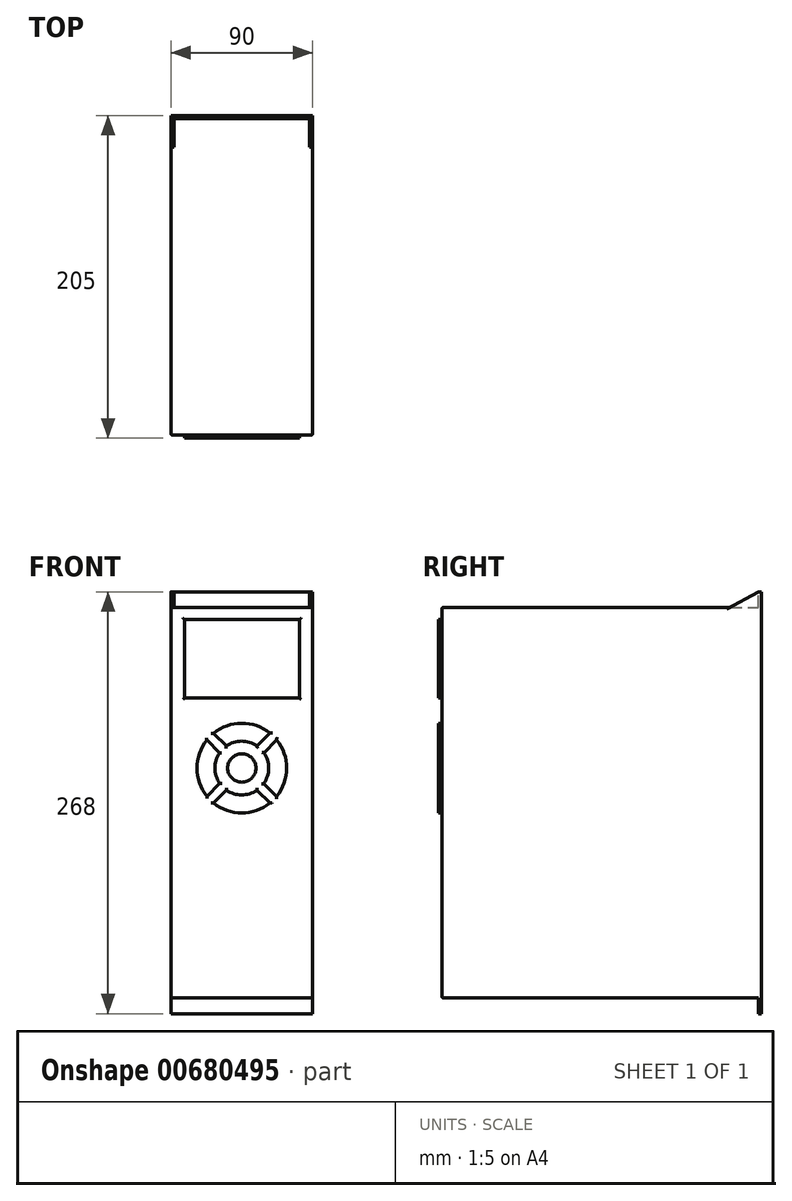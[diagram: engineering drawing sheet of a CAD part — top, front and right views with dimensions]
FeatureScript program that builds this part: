
annotation { "Feature Type Name" : "Feature", "Feature Type Description" : "" }
export const myFeature = defineFeature(function(context is Context, id is Id, definition is map)
    precondition{}
    {
        {
            var Q0;
            Q0=qCreatedBy(makeId("Front.planeOp"),FACE);
            var sketch = newSketch(context, id + "F0", { "sketchPlane" : qUnion([Q0])});
            skLineSegment(sketch, "E0.bottom", {"start": v(45, 124) * mm, "end": v(-45, 124) * mm});
            skLineSegment(sketch, "E0.top", {"start": v(45, -124) * mm, "end": v(-45, -124) * mm});
            skLineSegment(sketch, "E0.left", {"start": v(45, 124) * mm, "end": v(45, -124) * mm});
            skLineSegment(sketch, "E0.right", {"start": v(-45, 124) * mm, "end": v(-45, -124) * mm});
            skPoint(sketch, "E0.middle", {"position": v(0, 0) * mm});
            skSolve(sketch);
        }
        {
            var Q0;
            Q0=makeQuery(id+"F0.imprint","IMPRINT",FACE,{"disambiguationData":[TD([[makeQuery(id+"F0.imprint","IMPRINT",EDGE,{"derivedFrom":sQuery(id+"F0.wireOp",EDGE,"E0.bottom")}),1.0]])]});
            extrude(context, id + "F1", {"entities" : qUnion([Q0]), "depth" : 205 * mm, "offsetDistance" : 25 * mm});
        }
        {
            var Q0;
            Q0=makeQuery(id+"F1.opExtrude","CAP_FACE",FACE,{"disambiguationData":[OSD([sQuery(id+"F0.wireOp",EDGE,"E0.bottom"),sQuery(id+"F0.wireOp",EDGE,"E0.top"),sQuery(id+"F0.wireOp",EDGE,"E0.left"),sQuery(id+"F0.wireOp",EDGE,"E0.right")])],"isStart":false});
            var sketch = newSketch(context, id + "F2", { "sketchPlane" : qUnion([Q0])});
            skLineSegment(sketch, "E1.bottom", {"start": v(-36.41, 116.3) * mm, "end": v(36.68, 116.3) * mm});
            skLineSegment(sketch, "E1.top", {"start": v(-36.41, 66.5) * mm, "end": v(36.68, 66.5) * mm});
            skLineSegment(sketch, "E1.left", {"start": v(-36.41, 116.3) * mm, "end": v(-36.41, 66.5) * mm});
            skLineSegment(sketch, "E1.right", {"start": v(36.68, 116.3) * mm, "end": v(36.68, 66.5) * mm});
            skArc(sketch, "E2", {"start": v(-22.23, 39.81) * mm, "mid": v(-28.49, 21.94) * mm, "end": v(-22.15, 4.09) * mm});
            skLineSegment(sketch, "E3.0", {"start": v(22.18, 3.89) * mm, "end": v(13.93, 12.13) * mm});
            skLineSegment(sketch, "E4.0", {"start": v(17.93, -0.36) * mm, "end": v(9.66, 7.92) * mm});
            skLineSegment(sketch, "E5.0", {"start": v(-18.11, -0.36) * mm, "end": v(-9.76, 8) * mm});
            skLineSegment(sketch, "E6.0", {"start": v(-22.36, 3.89) * mm, "end": v(-14, 12.24) * mm});
            skArc(sketch, "E7.trimOffspring", {"start": v(17.91, 44.15) * mm, "mid": v(-0.06, 50.49) * mm, "end": v(-18, 44.07) * mm});
            skArc(sketch, "E8.trimOffspring", {"start": v(-17.91, -0.15) * mm, "mid": v(-0.06, -6.49) * mm, "end": v(17.81, -0.23) * mm});
            skArc(sketch, "E9.trimOffspring", {"start": v(22.07, 4) * mm, "mid": v(28.49, 21.94) * mm, "end": v(22.15, 39.91) * mm});
            skLineSegment(sketch, "E10.trimOffspring", {"start": v(-14.08, 31.66) * mm, "end": v(-22.36, 39.93) * mm});
            skLineSegment(sketch, "E11.trimOffspring", {"start": v(14, 31.76) * mm, "end": v(22.18, 39.93) * mm});
            skLineSegment(sketch, "E12.trimOffspring", {"start": v(9.76, 36) * mm, "end": v(17.93, 44.18) * mm});
            skLineSegment(sketch, "E13.trimOffspring", {"start": v(-9.87, 35.93) * mm, "end": v(-18.11, 44.18) * mm});
            skCircle(sketch, "E14", {"center": v(0, 22) * mm, "radius": 9 * mm});
            skArc(sketch, "E15", {"start": v(-14.08, 31.66) * mm, "mid": v(-17.07, 21.94) * mm, "end": v(-14, 12.24) * mm});
            skArc(sketch, "E16.trimOffspring", {"start": v(-9.76, 8) * mm, "mid": v(-0.06, 4.93) * mm, "end": v(9.66, 7.92) * mm});
            skArc(sketch, "E17.trimOffspring", {"start": v(13.93, 12.13) * mm, "mid": v(17.07, 21.94) * mm, "end": v(14, 31.76) * mm});
            skArc(sketch, "E18.trimOffspring", {"start": v(9.76, 36) * mm, "mid": v(-0.06, 39.07) * mm, "end": v(-9.87, 35.93) * mm});
            skSolve(sketch);
        }
        {
            var Q0;
            Q0=makeQuery(id+"F2.imprint","IMPRINT",FACE,{"disambiguationData":[TD([[makeQuery(id+"F2.imprint","IMPRINT",EDGE,{"derivedFrom":sQuery(id+"F2.wireOp",EDGE,"E1.bottom")}),1.0]])]});
            extrude(context, id + "F3", {"entities" : qUnion([Q0]), "operationType" : NewBodyOperationType.REMOVE, "oppositeDirection" : true, "depth" : 2 * mm, "offsetDistance" : 25 * mm});
        }
        {
            var Q0;
            Q0=makeQuery(id+"F1.opExtrude","CAP_FACE",FACE,{"disambiguationData":[OSD([sQuery(id+"F0.wireOp",EDGE,"E0.bottom"),sQuery(id+"F0.wireOp",EDGE,"E0.top"),sQuery(id+"F0.wireOp",EDGE,"E0.left"),sQuery(id+"F0.wireOp",EDGE,"E0.right")])],"isStart":true});
            var sketch = newSketch(context, id + "F4", { "sketchPlane" : qUnion([Q0])});
            skLineSegment(sketch, "E19.bottom", {"start": v(45, 134) * mm, "end": v(-45, 134) * mm});
            skLineSegment(sketch, "E19.top", {"start": v(45, -134) * mm, "end": v(-45, -134) * mm});
            skLineSegment(sketch, "E19.left", {"start": v(45, 134) * mm, "end": v(45, -134) * mm});
            skLineSegment(sketch, "E19.right", {"start": v(-45, 134) * mm, "end": v(-45, -134) * mm});
            skPoint(sketch, "E19.middle", {"position": v(0, 0) * mm});
            skSolve(sketch);
        }
        {
            var Q0;
            {var subQ6=sQuery(id+"F4.wireOp",EDGE,"E19.bottom");Q0=makeQuery(id+"F4.imprint","IMPRINT",FACE,{"disambiguationData":[TD([[makeQuery(id+"F4.imprint","IMPRINT",EDGE,{"derivedFrom":subQ6}),1.0]])]});}
            var Q1;
            {var subQ6=sQuery(id+"F4.wireOp",EDGE,"E19.top");Q1=makeQuery(id+"F4.imprint","IMPRINT",FACE,{"disambiguationData":[TD([[makeQuery(id+"F4.imprint","IMPRINT",EDGE,{"derivedFrom":subQ6}),-1.0]])]});}
            extrude(context, id + "F5", {"entities" : qUnion([Q0, Q1]), "operationType" : NewBodyOperationType.ADD, "oppositeDirection" : true, "depth" : 20 * mm, "offsetDistance" : 25 * mm});
        }
        {
            var Q0;
            Q0=makeQuery(id+"F5.opExtrude","SWEPT_FACE",FACE,{"disambiguationData":[OSD([sQuery(id+"F4.wireOp",EDGE,"E19.bottom")])]});
            var sketch = newSketch(context, id + "F6", { "sketchPlane" : qUnion([Q0])});
            skLineSegment(sketch, "E20.bottom", {"start": v(-45, 0) * mm, "end": v(-43, 0) * mm});
            skLineSegment(sketch, "E20.top", {"start": v(-45, -2) * mm, "end": v(-43, -2) * mm});
            skLineSegment(sketch, "E20.left", {"start": v(-45, 0) * mm, "end": v(-45, -2) * mm});
            skLineSegment(sketch, "E20.right", {"start": v(-43, 0) * mm, "end": v(-43, -2) * mm});
            skLineSegment(sketch, "E21.bottom", {"start": v(45, -20) * mm, "end": v(43, -20) * mm});
            skLineSegment(sketch, "E21.top", {"start": v(45, -18) * mm, "end": v(43, -18) * mm});
            skLineSegment(sketch, "E21.left", {"start": v(45, -20) * mm, "end": v(45, -18) * mm});
            skLineSegment(sketch, "E21.right", {"start": v(43, -20) * mm, "end": v(43, -18) * mm});
            skLineSegment(sketch, "E22.bottom", {"start": v(-43, -2) * mm, "end": v(43, -2) * mm});
            skLineSegment(sketch, "E22.top", {"start": v(-43, -20) * mm, "end": v(43, -20) * mm});
            skLineSegment(sketch, "E22.left", {"start": v(-43, -2) * mm, "end": v(-43, -20) * mm});
            skLineSegment(sketch, "E22.right", {"start": v(43, -2) * mm, "end": v(43, -20) * mm});
            skSolve(sketch);
        }
        {
            var Q0;
            {var subQ2=sQuery(id+"F6.wireOp",EDGE,"E22.bottom");Q0=makeQuery(id+"F6.imprint","IMPRINT",FACE,{"disambiguationData":[TD([[makeQuery(id+"F6.imprint","IMPRINT",EDGE,{"derivedFrom":subQ2}),-1.0]])]});}
            var Q1;
            Q1=makeQuery(id+"F1.opExtrude","SWEPT_FACE",FACE,{"disambiguationData":[OSD([sQuery(id+"F0.wireOp",EDGE,"E0.bottom")])]});
            extrude(context, id + "F7", {"entities" : qUnion([Q0]), "operationType" : NewBodyOperationType.REMOVE, "endBound" : BoundingType.UP_TO_SURFACE, "oppositeDirection" : true, "depth" : 25 * mm, "endBoundEntityFace" : qUnion([Q1]), "offsetDistance" : 25 * mm});
        }
        {
            var Q0;
            {var subQ0=sQuery(id+"F4.wireOp",EDGE,"E19.right");Q0=makeQuery(id+"F5.boolean.opBoolean","MERGE",FACE,{"derivedFrom":[makeQuery(id+"F1.opExtrude","SWEPT_FACE",FACE,{"disambiguationData":[OSD([sQuery(id+"F0.wireOp",EDGE,"E0.left")])]}),makeQuery(id+"F5.opExtrude","SWEPT_FACE",FACE,{"disambiguationData":[OSD([subQ0]),TDD([makeQuery(id+"F4.imprint","IMPRINT",EDGE,{"disambiguationData":[TD([[makeQuery(id+"F4.imprint","INTERSECT",VERTEX,{"derivedFrom":[makeQuery(id+"F1.opExtrude","CAP_EDGE",EDGE,{"disambiguationData":[OSD([sQuery(id+"F0.wireOp",EDGE,"E0.bottom")])],"isStart":true}),subQ0]}),1.0]])],"derivedFrom":subQ0})])]}),makeQuery(id+"F5.opExtrude","SWEPT_FACE",FACE,{"disambiguationData":[OSD([subQ0]),TDD([makeQuery(id+"F4.imprint","IMPRINT",EDGE,{"disambiguationData":[TD([[makeQuery(id+"F4.imprint","INTERSECT",VERTEX,{"derivedFrom":[makeQuery(id+"F1.opExtrude","CAP_EDGE",EDGE,{"disambiguationData":[OSD([sQuery(id+"F0.wireOp",EDGE,"E0.top")])],"isStart":true}),subQ0]}),-1.0]])],"derivedFrom":subQ0})])]})]});}
            var sketch = newSketch(context, id + "F8", { "sketchPlane" : qUnion([Q0])});
            skLineSegment(sketch, "E23", {"start": v(-20, 124) * mm, "end": v(-2, 134) * mm});
            skLineSegment(sketch, "E24", {"start": v(-2, 134) * mm, "end": v(0, 134) * mm});
            skSolve(sketch);
        }
        {
            var Q0;
            {var subQ0=sQuery(id+"F8.wireOp",EDGE,"E23");Q0=makeQuery(id+"F8.imprint","IMPRINT",FACE,{"disambiguationData":[TD([[makeQuery(id+"F8.imprint","IMPRINT",EDGE,{"derivedFrom":subQ0}),1.0]])]});}
            extrude(context, id + "F9", {"entities" : qUnion([Q0]), "operationType" : NewBodyOperationType.REMOVE, "endBound" : BoundingType.THROUGH_ALL, "oppositeDirection" : true, "depth" : 25 * mm, "offsetDistance" : 25 * mm});
        }
        {
            var Q0;
            Q0=makeQuery(id+"F1.opExtrude","SWEPT_EDGE",EDGE,{"disambiguationData":[OSD([sQuery(id+"F0.wireOp",EDGE,"E0.bottom"),sQuery(id+"F0.wireOp",EDGE,"E0.right")])]});
            var Q1;
            {var subQ0=sQuery(id+"F4.wireOp",EDGE,"E19.left");Q1=makeQuery(id+"F9.boolean.opBoolean","INTERSECT",EDGE,{"derivedFrom":[makeQuery(id+"F5.boolean.opBoolean","MERGE",FACE,{"derivedFrom":[makeQuery(id+"F1.opExtrude","SWEPT_FACE",FACE,{"disambiguationData":[OSD([sQuery(id+"F0.wireOp",EDGE,"E0.right")])]}),makeQuery(id+"F5.opExtrude","SWEPT_FACE",FACE,{"disambiguationData":[OSD([subQ0]),TDD([makeQuery(id+"F4.imprint","IMPRINT",EDGE,{"disambiguationData":[TD([[makeQuery(id+"F4.imprint","INTERSECT",VERTEX,{"derivedFrom":[makeQuery(id+"F1.opExtrude","CAP_EDGE",EDGE,{"disambiguationData":[OSD([sQuery(id+"F0.wireOp",EDGE,"E0.bottom")])],"isStart":true}),subQ0]}),1.0]])],"derivedFrom":subQ0})])]}),makeQuery(id+"F5.opExtrude","SWEPT_FACE",FACE,{"disambiguationData":[OSD([subQ0]),TDD([makeQuery(id+"F4.imprint","IMPRINT",EDGE,{"disambiguationData":[TD([[makeQuery(id+"F4.imprint","INTERSECT",VERTEX,{"derivedFrom":[makeQuery(id+"F1.opExtrude","CAP_EDGE",EDGE,{"disambiguationData":[OSD([sQuery(id+"F0.wireOp",EDGE,"E0.top")])],"isStart":true}),subQ0]}),-1.0]])],"derivedFrom":subQ0})])]})]}),makeQuery(id+"F9.opExtrude","SWEPT_FACE",FACE,{"disambiguationData":[OSD([sQuery(id+"F8.wireOp",EDGE,"E23")])]})]});}
            var Q2;
            Q2=makeQuery(id+"F9.boolean.opBoolean","COPY",EDGE,{"derivedFrom":makeQuery(id+"F9.opExtrude","CAP_EDGE",EDGE,{"disambiguationData":[OSD([sQuery(id+"F8.wireOp",EDGE,"E23")])],"isStart":true})});
            var Q3;
            Q3=makeQuery(id+"F1.opExtrude","SWEPT_EDGE",EDGE,{"disambiguationData":[OSD([sQuery(id+"F0.wireOp",EDGE,"E0.bottom"),sQuery(id+"F0.wireOp",EDGE,"E0.left")])]});
            var Q4;
            Q4=makeQuery(id+"F3.boolean.opBoolean","COPY",FACE,{"derivedFrom":makeQuery(id+"F3.opExtrude","CAP_FACE",FACE,{"disambiguationData":[OSD([sQuery(id+"F0.wireOp",EDGE,"E0.bottom"),sQuery(id+"F0.wireOp",EDGE,"E0.top"),sQuery(id+"F0.wireOp",EDGE,"E0.left"),sQuery(id+"F0.wireOp",EDGE,"E0.right"),sQuery(id+"F2.wireOp",EDGE,"E1.bottom"),sQuery(id+"F2.wireOp",EDGE,"E1.top"),sQuery(id+"F2.wireOp",EDGE,"E1.left"),sQuery(id+"F2.wireOp",EDGE,"E1.right"),sQuery(id+"F2.wireOp",EDGE,"E2"),sQuery(id+"F2.wireOp",EDGE,"E3.0"),sQuery(id+"F2.wireOp",EDGE,"E4.0"),sQuery(id+"F2.wireOp",EDGE,"E5.0"),sQuery(id+"F2.wireOp",EDGE,"E6.0"),sQuery(id+"F2.wireOp",EDGE,"E7.trimOffspring"),sQuery(id+"F2.wireOp",EDGE,"E8.trimOffspring"),sQuery(id+"F2.wireOp",EDGE,"E9.trimOffspring"),sQuery(id+"F2.wireOp",EDGE,"E10.trimOffspring"),sQuery(id+"F2.wireOp",EDGE,"E11.trimOffspring"),sQuery(id+"F2.wireOp",EDGE,"E12.trimOffspring"),sQuery(id+"F2.wireOp",EDGE,"E13.trimOffspring"),sQuery(id+"F2.wireOp",EDGE,"E14"),sQuery(id+"F2.wireOp",EDGE,"E15"),sQuery(id+"F2.wireOp",EDGE,"E16.trimOffspring"),sQuery(id+"F2.wireOp",EDGE,"E17.trimOffspring"),sQuery(id+"F2.wireOp",EDGE,"E18.trimOffspring")])],"isStart":false})});
            fillet(context, id + "F10", {"entities" : qUnion([Q0, Q1, Q2, Q3, Q4]), "radius" : 1 * mm, "tangentPropagation" : true, "allowEdgeOverflow" : false});
        }
        {
            var Q0;
            Q0=makeQuery(id+"F5.opExtrude","CAP_FACE",FACE,{"disambiguationData":[OSD([sQuery(id+"F0.wireOp",EDGE,"E0.top"),sQuery(id+"F4.wireOp",EDGE,"E19.top"),sQuery(id+"F4.wireOp",EDGE,"E19.left"),sQuery(id+"F4.wireOp",EDGE,"E19.right")])],"isStart":false});
            extrude(context, id + "F11", {"entities" : qUnion([Q0]), "operationType" : NewBodyOperationType.REMOVE, "oppositeDirection" : true, "depth" : 18 * mm, "offsetDistance" : 25 * mm});
        }
    });
